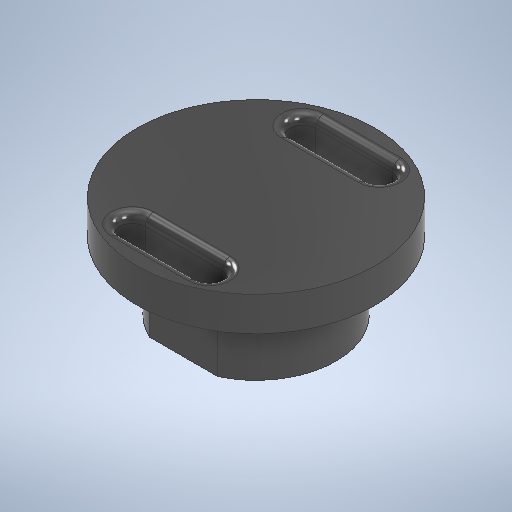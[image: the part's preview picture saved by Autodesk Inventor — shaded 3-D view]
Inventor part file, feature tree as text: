
AUTODESK INVENTOR PART (.ipt)
format: ipt  version: 2025.2 (Build 292293000, 293)  size: 281,600 bytes
history: native  units: in
note: dims shown in document units (in); Inventor stores cm internally (conversion verified against a paired STEP export)
features: extrude x3, sketch x3, fillet x1
ambient origin geometry x8: Origin, YZ Plane, XZ Plane, XY Plane, X Axis, Y Axis, Z Axis, Center Point
bodies: Solid1 (feature_tree)
feature tree (7):
  extrude  "Extrusion1"  Depth=0.4in TaperAngle=0.0deg
  extrude  "Extrusion2"  Depth=0.2in TaperAngle=0.0deg
  extrude  "Extrusion3"  Depth=0.05in
  fillet  "Fillet1"  Radius=0.15in
  sketch  "Sketch1"  dims[d0=0.94in d1=0.4in d2=0.0in]
  sketch  "Sketch2"  dims[d3=1.4in d4=0.2in d5=0.0in]
  sketch  "Sketch3"  dims[d6=0.0in d7=0.3in d8=0.15in d9=0.15in d10=0.5in d11=0.3in d12=0.3in d13=0.5in d14=0.6in d15=0.0in d16=0.05in]
